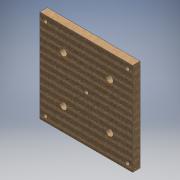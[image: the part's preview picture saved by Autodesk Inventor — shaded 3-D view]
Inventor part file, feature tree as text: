
AUTODESK INVENTOR PART (.ipt)
format: ipt  version: 2016 (Build 200138000, 138)  size: 164,864 bytes
history: native  units: mm
features: extrude x1, sketch x1
ambient origin geometry x8: Origin, YZ Plane, XZ Plane, XY Plane, X Axis, Y Axis, Z Axis, Center Point
bodies: Body1 (feature_tree)
feature tree (2):
  extrude  "Extrusion3"  Depth=80.0mm
  sketch  "Sketch1"  dims[d0=36.2235mm d1=80.0mm d2=80.0mm d13=3.43mm d14=3.43mm d15=50.0mm d16=6.3mm d17=6.39mm d18=0.0mm]
